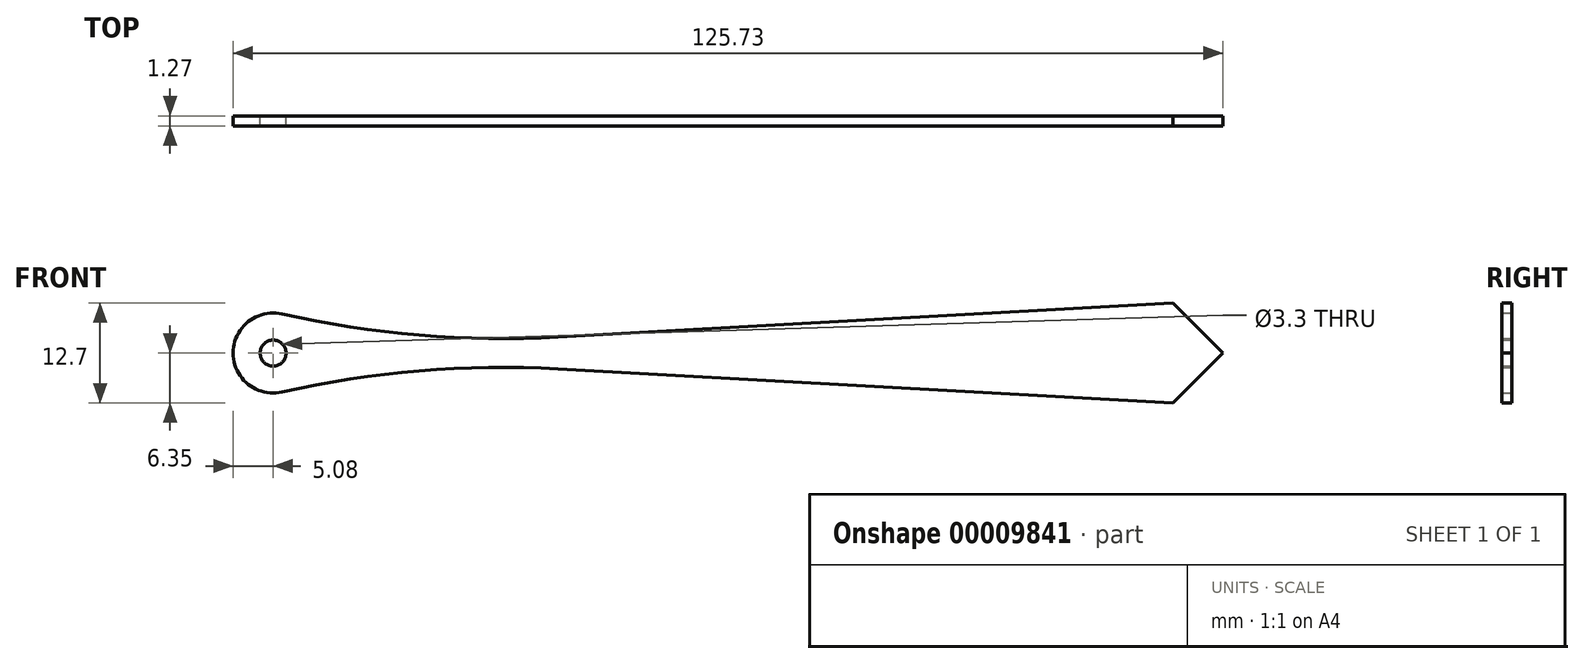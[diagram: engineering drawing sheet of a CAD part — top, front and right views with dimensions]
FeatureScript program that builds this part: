
annotation { "Feature Type Name" : "Feature", "Feature Type Description" : "" }
export const myFeature = defineFeature(function(context is Context, id is Id, definition is map)
    precondition{}
    {
        {
            var Q0;
            Q0=qCreatedBy(makeId("Front.planeOp"),FACE);
            var sketch = newSketch(context, id + "F0", { "sketchPlane" : qUnion([Q0])});
            skArc(sketch, "E0", {"start": v(5.07, 0.28) * mm, "mid": v(-5.08, 0) * mm, "end": v(5.07, -0.28) * mm});
            skLineSegment(sketch, "E1", {"start": v(5.07, 0.28) * mm, "end": v(114.3, 6.35) * mm});
            skLineSegment(sketch, "E2", {"start": v(5.07, -0.28) * mm, "end": v(114.3, -6.35) * mm});
            skLineSegment(sketch, "E3", {"start": v(0, 0) * mm, "end": v(114.3, 0) * mm, "construction": true});
            skCircle(sketch, "E4", {"center": v(0, 0) * mm, "radius": 1.65 * mm});
            skLineSegment(sketch, "E5", {"start": v(114.3, 6.35) * mm, "end": v(114.3, -6.35) * mm, "construction": true});
            skLineSegment(sketch, "E6", {"start": v(114.3, 6.35) * mm, "end": v(120.65, 0) * mm});
            skLineSegment(sketch, "E7", {"start": v(120.65, 0) * mm, "end": v(114.3, -6.35) * mm});
            skSolve(sketch);
        }
        {
            var Q0;
            {var subQ3=sQuery(id+"F0.wireOp",EDGE,"E1");var subQ5=sQuery(id+"F0.wireOp",EDGE,"E0");var subQ7=makeQuery(id+"F0.imprint","INTERSECT",VERTEX,{"derivedFrom":[subQ5,subQ3]});Q0=makeQuery(id+"F0.imprint","IMPRINT",FACE,{"disambiguationData":[TD([[makeQuery(id+"F0.imprint","IMPRINT",EDGE,{"disambiguationData":[TD([[subQ7,-1.0]])],"derivedFrom":subQ5}),1.0]])]});}
            var Q1;
            {var subQ1=sQuery(id+"F0.wireOp",EDGE,"E0");var subQ5=sQuery(id+"F0.wireOp",EDGE,"E1");var subQ6=makeQuery(id+"F0.imprint","INTERSECT",VERTEX,{"derivedFrom":[subQ1,subQ5]});Q1=makeQuery(id+"F0.imprint","IMPRINT",FACE,{"disambiguationData":[TD([[makeQuery(id+"F0.imprint","IMPRINT",EDGE,{"disambiguationData":[TD([[subQ6,1.0]])],"derivedFrom":subQ1}),-1.0]])]});}
            var Q2;
            {var subQ3=sQuery(id+"F0.wireOp",EDGE,"E1");var subQ5=sQuery(id+"F0.wireOp",EDGE,"E0");var subQ7=makeQuery(id+"F0.imprint","INTERSECT",VERTEX,{"derivedFrom":[subQ5,subQ3]});Q2=makeQuery(id+"F0.imprint","IMPRINT",FACE,{"disambiguationData":[TD([[makeQuery(id+"F0.imprint","IMPRINT",EDGE,{"disambiguationData":[TD([[subQ7,1.0]])],"derivedFrom":subQ5}),1.0]])]});}
            var Q3;
            {var subQ0=sQuery(id+"F0.wireOp",EDGE,"40b92105-6876-4540-b0be-2552fa4ecd17");var subQ2=makeQuery(id+"F0.imprint","INTERSECT",VERTEX,{"derivedFrom":[subQ0,sQuery(id+"F0.wireOp",EDGE,"E1")]});Q3=makeQuery(id+"F0.imprint","IMPRINT",FACE,{"disambiguationData":[TD([[makeQuery(id+"F0.imprint","IMPRINT",EDGE,{"disambiguationData":[TD([[subQ2,-1.0]])],"derivedFrom":subQ0}),1.0]])]});}
            var Q4;
            Q4=makeQuery(id+"F0.imprint","IMPRINT",FACE,{"disambiguationData":[TD([[makeQuery(id+"F0.imprint","IMPRINT",EDGE,{"derivedFrom":sQuery(id+"F0.wireOp",EDGE,"E5")}),1.0]])]});
            extrude(context, id + "F1", {"entities" : qUnion([Q0, Q1, Q2, Q3, Q4]), "depth" : 1.27 * mm});
        }
        {
            var Q0;
            Q0=makeQuery(id+"F1.opExtrude","SWEPT_EDGE",EDGE,{"disambiguationData":[OSD([sQuery(id+"F0.wireOp",EDGE,"E0"),sQuery(id+"F0.wireOp",EDGE,"E1")])]});
            var Q1;
            Q1=makeQuery(id+"F1.opExtrude","SWEPT_EDGE",EDGE,{"disambiguationData":[OSD([sQuery(id+"F0.wireOp",EDGE,"E0"),sQuery(id+"F0.wireOp",EDGE,"E2")])]});
            fillet(context, id + "F2", {"entities" : qUnion([Q0, Q1]), "radius" : 127 * mm, "tangentPropagation" : true, "allowEdgeOverflow" : false});
        }
    });
